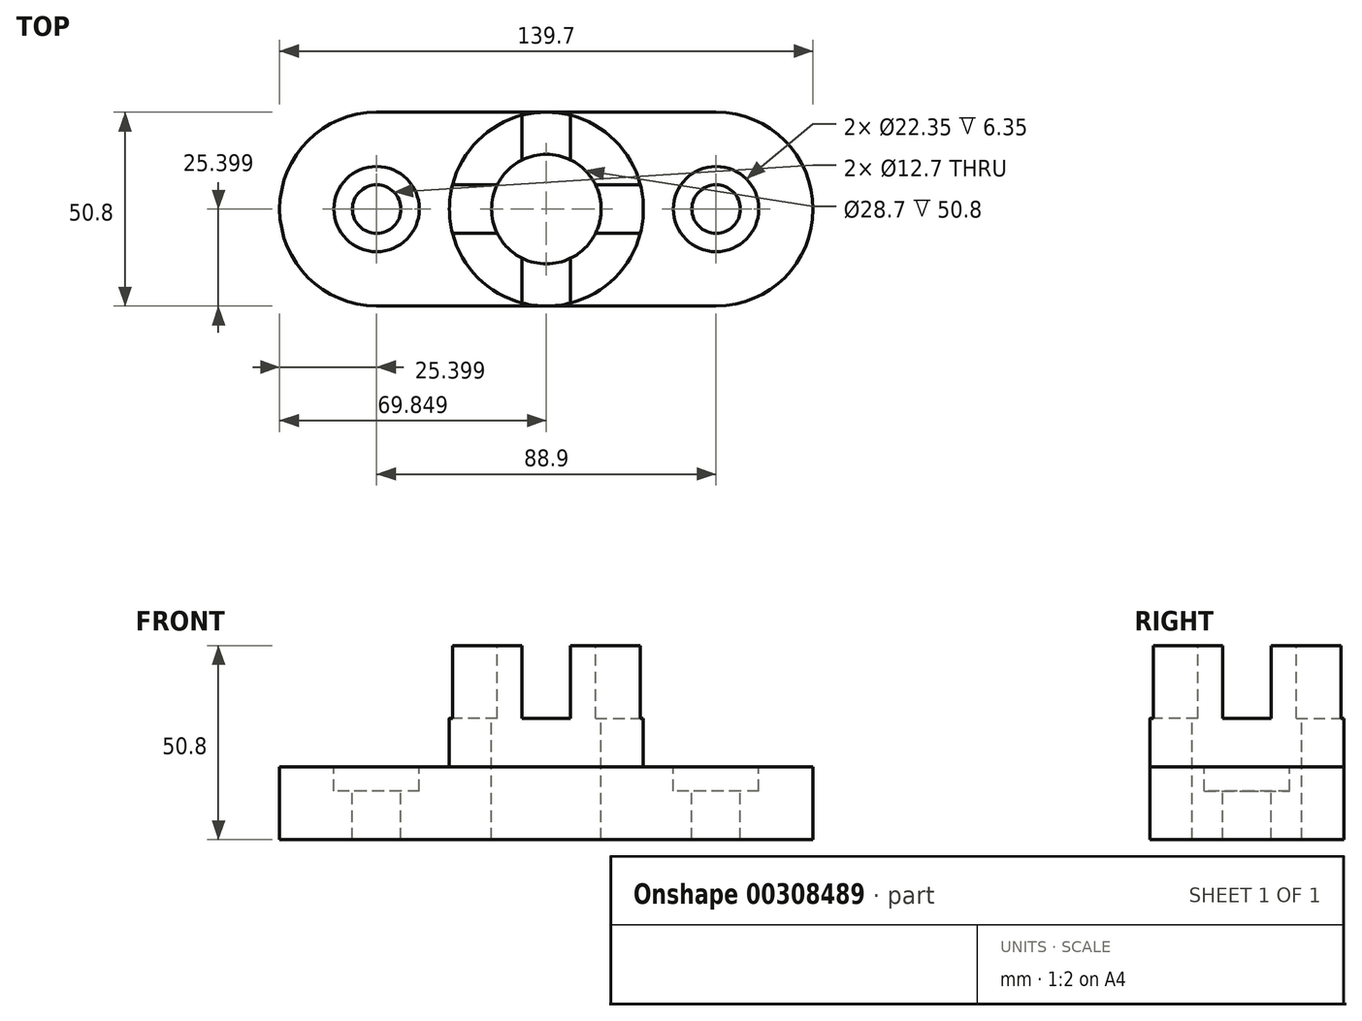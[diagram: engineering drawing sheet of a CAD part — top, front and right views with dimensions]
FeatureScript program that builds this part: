
annotation { "Feature Type Name" : "Feature", "Feature Type Description" : "" }
export const myFeature = defineFeature(function(context is Context, id is Id, definition is map)
    precondition{}
    {
        {
            var Q0;
            Q0=qCreatedBy(makeId("Top.planeOp"),FACE);
            var sketch = newSketch(context, id + "F0", { "sketchPlane" : qUnion([Q0])});
            skCircle(sketch, "E0", {"center": v(-41.94, 31.94) * mm, "radius": 25.4 * mm});
            skCircle(sketch, "E1", {"center": v(46.96, 31.94) * mm, "radius": 25.4 * mm});
            skLineSegment(sketch, "E2", {"start": v(-41.94, 57.34) * mm, "end": v(46.96, 57.34) * mm});
            skLineSegment(sketch, "E3", {"start": v(-41.94, 6.54) * mm, "end": v(46.96, 6.54) * mm});
            skSolve(sketch);
        }
        {
            var Q0;
            {var subQ0=sQuery(id+"F0.wireOp",EDGE,"E2");Q0=makeQuery(id+"F0.imprint","IMPRINT",FACE,{"disambiguationData":[TD([[makeQuery(id+"F0.imprint","IMPRINT",EDGE,{"derivedFrom":subQ0}),-1.0]])]});}
            var Q1;
            {var subQ0=sQuery(id+"F0.wireOp",EDGE,"E0");var subQ1=makeQuery(id+"F0.imprint","INTERSECT",VERTEX,{"derivedFrom":[subQ0,sQuery(id+"F0.wireOp",EDGE,"E2")]});Q1=makeQuery(id+"F0.imprint","IMPRINT",FACE,{"disambiguationData":[TD([[makeQuery(id+"F0.imprint","IMPRINT",EDGE,{"disambiguationData":[TD([[subQ1,-1.0]])],"derivedFrom":subQ0}),1.0]])]});}
            var Q2;
            {var subQ0=sQuery(id+"F0.wireOp",EDGE,"E1");var subQ1=makeQuery(id+"F0.imprint","INTERSECT",VERTEX,{"derivedFrom":[subQ0,sQuery(id+"F0.wireOp",EDGE,"E2")]});Q2=makeQuery(id+"F0.imprint","IMPRINT",FACE,{"disambiguationData":[TD([[makeQuery(id+"F0.imprint","IMPRINT",EDGE,{"disambiguationData":[TD([[subQ1,-1.0]])],"derivedFrom":subQ0}),1.0]])]});}
            extrude(context, id + "F1", {"entities" : qUnion([Q0, Q1, Q2]), "oppositeDirection" : true, "depth" : 19.05 * mm});
        }
        {
            var Q0;
            Q0=makeQuery(id+"F1.opExtrude","CAP_FACE",FACE,{"disambiguationData":[OSD([sQuery(id+"F0.wireOp",EDGE,"E0"),sQuery(id+"F0.wireOp",EDGE,"E1"),sQuery(id+"F0.wireOp",EDGE,"E2"),sQuery(id+"F0.wireOp",EDGE,"E3")])],"isStart":true});
            var sketch = newSketch(context, id + "F2", { "sketchPlane" : qUnion([Q0])});
            skCircle(sketch, "E4", {"center": v(-41.94, 31.94) * mm, "radius": 11.18 * mm});
            skCircle(sketch, "E5", {"center": v(46.96, 31.94) * mm, "radius": 11.18 * mm});
            skSolve(sketch);
        }
        {
            var Q0;
            Q0 = qSketchRegion(id + "F2", true);
            extrude(context, id + "F3", {"entities" : qUnion([Q0]), "operationType" : NewBodyOperationType.REMOVE, "oppositeDirection" : true, "depth" : 6.35 * mm});
        }
        {
            var Q0;
            Q0=makeQuery(id+"F1.opExtrude","CAP_FACE",FACE,{"disambiguationData":[OSD([sQuery(id+"F0.wireOp",EDGE,"E0"),sQuery(id+"F0.wireOp",EDGE,"E1"),sQuery(id+"F0.wireOp",EDGE,"E2"),sQuery(id+"F0.wireOp",EDGE,"E3")])],"isStart":true});
            var sketch = newSketch(context, id + "F4", { "sketchPlane" : qUnion([Q0])});
            skCircle(sketch, "E6", {"center": v(-41.94, 31.94) * mm, "radius": 6.35 * mm});
            skCircle(sketch, "E7", {"center": v(46.96, 31.94) * mm, "radius": 6.35 * mm});
            skSolve(sketch);
        }
        {
            var Q0;
            Q0 = qSketchRegion(id + "F4", true);
            extrude(context, id + "F5", {"entities" : qUnion([Q0]), "operationType" : NewBodyOperationType.REMOVE, "endBound" : BoundingType.THROUGH_ALL, "oppositeDirection" : true, "depth" : 25.4 * mm});
        }
        {
            var Q0;
            Q0=makeQuery(id+"F1.opExtrude","CAP_FACE",FACE,{"disambiguationData":[OSD([sQuery(id+"F0.wireOp",EDGE,"E0"),sQuery(id+"F0.wireOp",EDGE,"E1"),sQuery(id+"F0.wireOp",EDGE,"E2"),sQuery(id+"F0.wireOp",EDGE,"E3")])],"isStart":true});
            var sketch = newSketch(context, id + "F6", { "sketchPlane" : qUnion([Q0])});
            skCircle(sketch, "E8", {"center": v(2.5, 31.94) * mm, "radius": 25.4 * mm});
            skPoint(sketch, "E8.centerSnap0", {"position": v(72.36, 31.94) * mm});
            skPoint(sketch, "E8.centerSnap1", {"position": v(2.5, 57.34) * mm});
            skSolve(sketch);
        }
        {
            var Q0;
            Q0 = qSketchRegion(id + "F6", true);
            extrude(context, id + "F7", {"entities" : qUnion([Q0]), "operationType" : NewBodyOperationType.ADD, "depth" : 31.75 * mm});
        }
        {
            var Q0;
            Q0=makeQuery(id+"F7.opExtrude","CAP_FACE",FACE,{"disambiguationData":[OSD([sQuery(id+"F6.wireOp",EDGE,"E8")])],"isStart":false});
            var sketch = newSketch(context, id + "F8", { "sketchPlane" : qUnion([Q0])});
            skCircle(sketch, "E9", {"center": v(2.5, 31.94) * mm, "radius": 14.35 * mm});
            skSolve(sketch);
        }
        {
            var Q0;
            Q0 = qSketchRegion(id + "F8", true);
            extrude(context, id + "F9", {"entities" : qUnion([Q0]), "operationType" : NewBodyOperationType.REMOVE, "endBound" : BoundingType.THROUGH_ALL, "oppositeDirection" : true, "depth" : 25.4 * mm});
        }
        {
            var Q0;
            Q0=makeQuery(id+"F7.opExtrude","CAP_FACE",FACE,{"disambiguationData":[OSD([sQuery(id+"F6.wireOp",EDGE,"E8")])],"isStart":false});
            var sketch = newSketch(context, id + "F10", { "sketchPlane" : qUnion([Q0])});
            skLineSegment(sketch, "E10", {"start": v(2.5, 31.94) * mm, "end": v(2.5, 57.34) * mm});
            skLineSegment(sketch, "E11", {"start": v(2.5, 57.34) * mm, "end": v(8.86, 57.34) * mm});
            skLineSegment(sketch, "E12", {"start": v(8.86, 57.34) * mm, "end": v(8.86, 6.54) * mm});
            skLineSegment(sketch, "E13", {"start": v(8.86, 6.54) * mm, "end": v(-3.84, 6.54) * mm});
            skLineSegment(sketch, "E14", {"start": v(-3.84, 6.54) * mm, "end": v(-3.84, 57.34) * mm});
            skLineSegment(sketch, "E15", {"start": v(-3.84, 57.34) * mm, "end": v(2.5, 57.34) * mm});
            skSolve(sketch);
        }
        {
            var Q0;
            Q0 = qSketchRegion(id + "F10", true);
            extrude(context, id + "F11", {"entities" : qUnion([Q0]), "operationType" : NewBodyOperationType.REMOVE, "oppositeDirection" : true, "depth" : 19.05 * mm});
        }
        {
            var Q0;
            {var subQ0=sQuery(id+"F6.wireOp",EDGE,"E8");Q0=makeQuery(id+"F11.boolean.opBoolean","SPLIT",FACE,{"disambiguationData":[TD([makeQuery(id+"F11.opExtrude","SWEPT_FACE",FACE,{"disambiguationData":[OSD([sQuery(id+"F10.wireOp",EDGE,"E12")])]})])],"derivedFrom":makeQuery(id+"F7.opExtrude","CAP_FACE",FACE,{"disambiguationData":[OSD([subQ0])],"isStart":false})});}
            var sketch = newSketch(context, id + "F12", { "sketchPlane" : qUnion([Q0])});
            skLineSegment(sketch, "E16", {"start": v(2.5, 31.94) * mm, "end": v(27.9, 31.94) * mm});
            skLineSegment(sketch, "E17", {"start": v(27.9, 31.94) * mm, "end": v(27.9, 25.59) * mm});
            skLineSegment(sketch, "E18", {"start": v(27.9, 25.59) * mm, "end": v(-22.9, 25.59) * mm});
            skLineSegment(sketch, "E19", {"start": v(-22.9, 25.59) * mm, "end": v(-22.9, 38.29) * mm});
            skLineSegment(sketch, "E20", {"start": v(-22.9, 38.29) * mm, "end": v(27.9, 38.29) * mm});
            skLineSegment(sketch, "E21", {"start": v(27.9, 38.29) * mm, "end": v(27.9, 31.94) * mm});
            skSolve(sketch);
        }
        {
            var Q0;
            Q0 = qSketchRegion(id + "F12", true);
            extrude(context, id + "F13", {"entities" : qUnion([Q0]), "operationType" : NewBodyOperationType.REMOVE, "oppositeDirection" : true, "depth" : 19.05 * mm});
        }
    });
